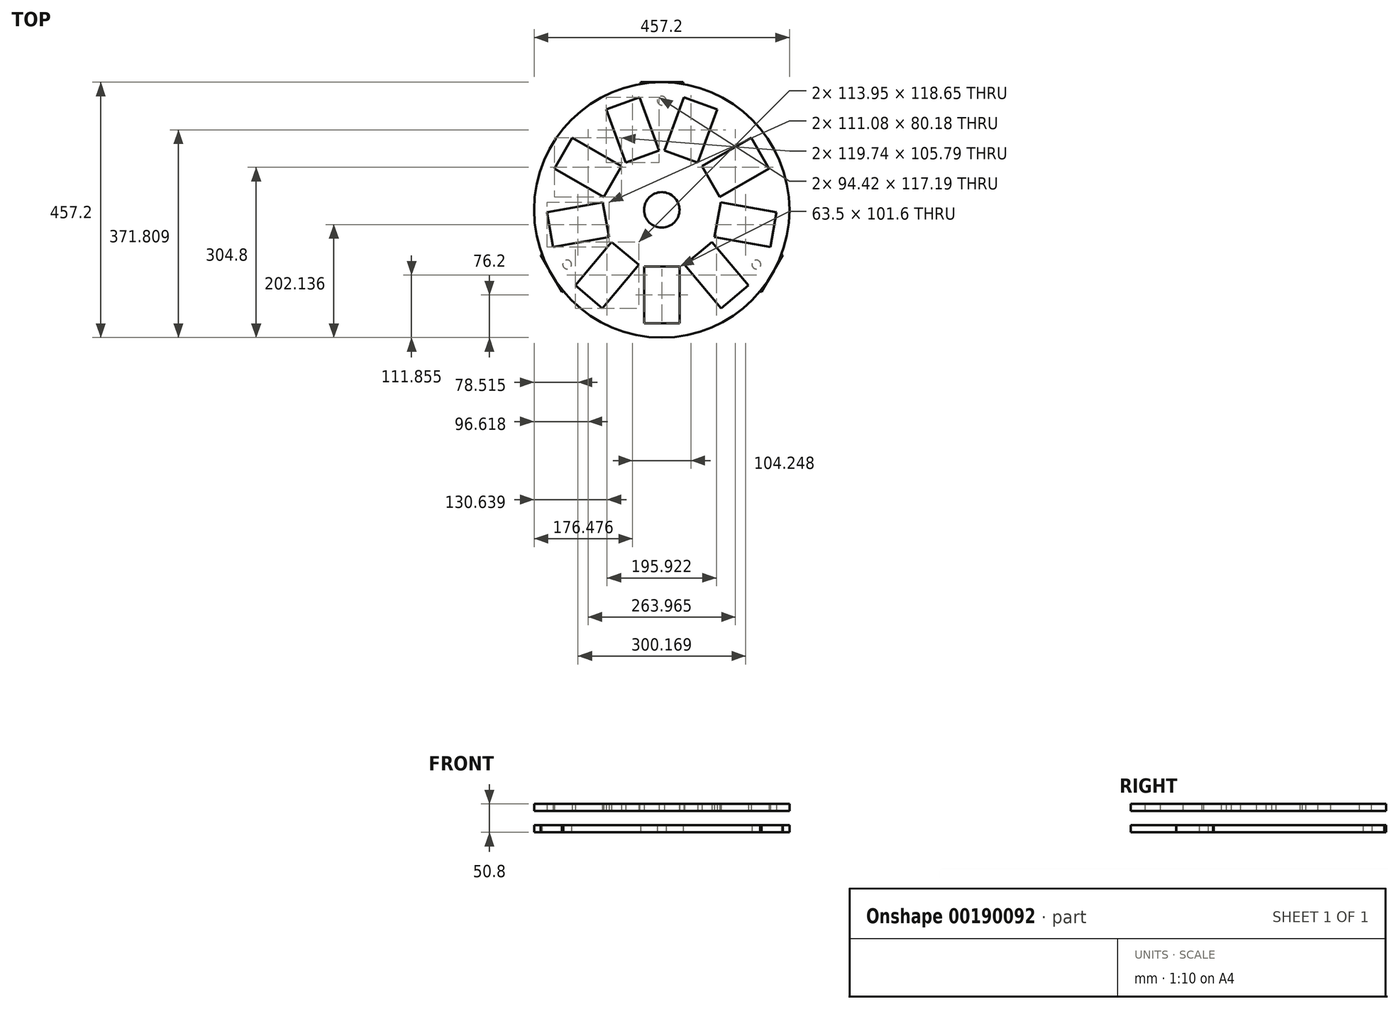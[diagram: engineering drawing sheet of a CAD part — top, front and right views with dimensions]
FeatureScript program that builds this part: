
annotation { "Feature Type Name" : "Feature", "Feature Type Description" : "" }
export const myFeature = defineFeature(function(context is Context, id is Id, definition is map)
    precondition{}
    {
        {
            var Q0;
            Q0=qCreatedBy(makeId("Top.planeOp"),FACE);
            var sketch = newSketch(context, id + "F0", { "sketchPlane" : qUnion([Q0])});
            skArc(sketch, "E0", {"start": v(-38.1, 147.56) * mm, "mid": v(-131.98, 76.2) * mm, "end": v(-146.84, -40.78) * mm});
            skLineSegment(sketch, "E1.top", {"start": v(-38.1, 228.6) * mm, "end": v(38.1, 228.6) * mm});
            skLineSegment(sketch, "E1.left", {"start": v(-38.1, 147.56) * mm, "end": v(-38.1, 228.6) * mm});
            skLineSegment(sketch, "E1.right", {"start": v(38.1, 147.56) * mm, "end": v(38.1, 228.6) * mm});
            skCircle(sketch, "E2", {"center": v(0, 195.58) * mm, "radius": 7.94 * mm});
            skPoint(sketch, "E1.bottom.start.orphan", {"position": v(-38.1, 0) * mm});
            skLineSegment(sketch, "E3.1.0", {"start": v(-178.92, -147.3) * mm, "end": v(-217.02, -81.3) * mm});
            skCircle(sketch, "E3.1.1", {"center": v(-169.38, -97.79) * mm, "radius": 7.94 * mm});
            skLineSegment(sketch, "E3.1.2", {"start": v(-146.84, -40.78) * mm, "end": v(-217.02, -81.3) * mm});
            skLineSegment(sketch, "E3.1.3", {"start": v(-108.74, -106.78) * mm, "end": v(-178.92, -147.3) * mm});
            skLineSegment(sketch, "E3.2.0", {"start": v(217.02, -81.3) * mm, "end": v(178.92, -147.3) * mm});
            skCircle(sketch, "E3.2.1", {"center": v(169.38, -97.8) * mm, "radius": 7.94 * mm});
            skLineSegment(sketch, "E3.2.2", {"start": v(108.74, -106.78) * mm, "end": v(178.92, -147.3) * mm});
            skLineSegment(sketch, "E3.2.3", {"start": v(146.84, -40.78) * mm, "end": v(217.02, -81.3) * mm});
            skArc(sketch, "E4.trimOffspring", {"start": v(-108.74, -106.78) * mm, "mid": v(0, -152.4) * mm, "end": v(108.74, -106.78) * mm});
            skArc(sketch, "E5.trimOffspring", {"start": v(146.84, -40.78) * mm, "mid": v(131.98, 76.2) * mm, "end": v(38.1, 147.56) * mm});
            skCircle(sketch, "E6", {"center": v(0, 0) * mm, "radius": 228.6 * mm});
            skSolve(sketch);
        }
        {
            var Q0;
            Q0 = qSketchRegion(id + "F0", true);
            extrude(context, id + "F1", {"entities" : qUnion([Q0]), "depth" : 12.7 * mm});
        }
        {
            var Q0;
            Q0=makeQuery(id+"F1.opExtrude","CAP_FACE",FACE,{"disambiguationData":[OSD([sQuery(id+"F0.wireOp",EDGE,"E1.top"),sQuery(id+"F0.wireOp",EDGE,"E1.left"),sQuery(id+"F0.wireOp",EDGE,"E1.right"),sQuery(id+"F0.wireOp",EDGE,"E2"),sQuery(id+"F0.wireOp",EDGE,"E3.1.0"),sQuery(id+"F0.wireOp",EDGE,"E3.1.1"),sQuery(id+"F0.wireOp",EDGE,"E3.1.2"),sQuery(id+"F0.wireOp",EDGE,"E3.1.3"),sQuery(id+"F0.wireOp",EDGE,"E3.2.0"),sQuery(id+"F0.wireOp",EDGE,"E3.2.1"),sQuery(id+"F0.wireOp",EDGE,"E3.2.2"),sQuery(id+"F0.wireOp",EDGE,"E3.2.3"),sQuery(id+"F0.wireOp",EDGE,"E6")])],"isStart":false});
            var sketch = newSketch(context, id + "F2", { "sketchPlane" : qUnion([Q0])});
            skPoint(sketch, "E7.middle", {"position": v(39.44, 147.2) * mm});
            skLineSegment(sketch, "E8", {"start": v(26.3, 98.14) * mm, "end": v(-4.37, 106.36) * mm});
            skLineSegment(sketch, "E9", {"start": v(-4.37, 106.36) * mm, "end": v(21.92, 204.5) * mm});
            skLineSegment(sketch, "E10", {"start": v(21.92, 204.5) * mm, "end": v(83.26, 188.06) * mm});
            skLineSegment(sketch, "E11", {"start": v(83.26, 188.06) * mm, "end": v(56.96, 89.92) * mm});
            skLineSegment(sketch, "E12", {"start": v(56.96, 89.92) * mm, "end": v(56.96, 89.9) * mm});
            skLineSegment(sketch, "E13", {"start": v(56.96, 89.9) * mm, "end": v(26.3, 98.14) * mm});
            skLineSegment(sketch, "E14.1.0", {"start": v(-57.1, 197.58) * mm, "end": v(-14.16, 105.5) * mm});
            skLineSegment(sketch, "E14.1.1", {"start": v(-114.65, 170.74) * mm, "end": v(-57.1, 197.58) * mm});
            skLineSegment(sketch, "E14.1.2", {"start": v(-71.71, 78.66) * mm, "end": v(-114.65, 170.74) * mm});
            skLineSegment(sketch, "E14.1.3", {"start": v(-14.16, 105.48) * mm, "end": v(-42.94, 92.08) * mm});
            skLineSegment(sketch, "E14.1.4", {"start": v(-42.94, 92.08) * mm, "end": v(-71.71, 78.66) * mm});
            skLineSegment(sketch, "E14.2.0", {"start": v(-170.74, 114.65) * mm, "end": v(-78.66, 71.71) * mm});
            skLineSegment(sketch, "E14.2.1", {"start": v(-197.58, 57.1) * mm, "end": v(-170.74, 114.65) * mm});
            skLineSegment(sketch, "E14.2.2", {"start": v(-105.5, 14.16) * mm, "end": v(-197.58, 57.1) * mm});
            skLineSegment(sketch, "E14.2.3", {"start": v(-78.65, 71.7) * mm, "end": v(-92.08, 42.94) * mm});
            skLineSegment(sketch, "E14.2.4", {"start": v(-92.08, 42.94) * mm, "end": v(-105.5, 14.16) * mm});
            skLineSegment(sketch, "E14.3.0", {"start": v(-204.5, -21.92) * mm, "end": v(-106.36, 4.37) * mm});
            skLineSegment(sketch, "E14.3.1", {"start": v(-188.06, -83.26) * mm, "end": v(-204.5, -21.92) * mm});
            skLineSegment(sketch, "E14.3.2", {"start": v(-89.92, -56.96) * mm, "end": v(-188.06, -83.26) * mm});
            skLineSegment(sketch, "E14.3.3", {"start": v(-106.34, 4.38) * mm, "end": v(-98.14, -26.3) * mm});
            skLineSegment(sketch, "E14.3.4", {"start": v(-98.14, -26.3) * mm, "end": v(-89.92, -56.96) * mm});
            skLineSegment(sketch, "E14.4.0", {"start": v(-142.56, -148.24) * mm, "end": v(-84.28, -65.01) * mm});
            skLineSegment(sketch, "E14.4.1", {"start": v(-90.54, -184.66) * mm, "end": v(-142.56, -148.24) * mm});
            skLineSegment(sketch, "E14.4.2", {"start": v(-32.27, -101.44) * mm, "end": v(-90.54, -184.66) * mm});
            skLineSegment(sketch, "E14.4.3", {"start": v(-84.27, -65) * mm, "end": v(-58.28, -83.23) * mm});
            skLineSegment(sketch, "E14.4.4", {"start": v(-58.28, -83.23) * mm, "end": v(-32.27, -101.44) * mm});
            skLineSegment(sketch, "E14.5.0", {"start": v(-13.92, -205.2) * mm, "end": v(-22.77, -103.98) * mm});
            skLineSegment(sketch, "E14.5.1", {"start": v(49.34, -199.66) * mm, "end": v(-13.92, -205.2) * mm});
            skLineSegment(sketch, "E14.5.2", {"start": v(40.48, -98.45) * mm, "end": v(49.34, -199.66) * mm});
            skLineSegment(sketch, "E14.5.3", {"start": v(-22.78, -103.96) * mm, "end": v(8.86, -101.21) * mm});
            skLineSegment(sketch, "E14.5.4", {"start": v(8.86, -101.21) * mm, "end": v(40.48, -98.45) * mm});
            skLineSegment(sketch, "E14.6.0", {"start": v(121.23, -166.13) * mm, "end": v(49.4, -94.3) * mm});
            skLineSegment(sketch, "E14.6.1", {"start": v(166.13, -121.23) * mm, "end": v(121.23, -166.13) * mm});
            skLineSegment(sketch, "E14.6.2", {"start": v(94.3, -49.4) * mm, "end": v(166.13, -121.23) * mm});
            skLineSegment(sketch, "E14.6.3", {"start": v(49.38, -94.28) * mm, "end": v(71.84, -71.84) * mm});
            skLineSegment(sketch, "E14.6.4", {"start": v(71.84, -71.84) * mm, "end": v(94.3, -49.4) * mm});
            skLineSegment(sketch, "E14.7.0", {"start": v(199.66, -49.34) * mm, "end": v(98.45, -40.48) * mm});
            skLineSegment(sketch, "E14.7.1", {"start": v(205.2, 13.92) * mm, "end": v(199.66, -49.34) * mm});
            skLineSegment(sketch, "E14.7.2", {"start": v(103.98, 22.77) * mm, "end": v(205.2, 13.92) * mm});
            skLineSegment(sketch, "E14.7.3", {"start": v(98.43, -40.48) * mm, "end": v(101.21, -8.86) * mm});
            skLineSegment(sketch, "E14.7.4", {"start": v(101.21, -8.86) * mm, "end": v(103.98, 22.77) * mm});
            skLineSegment(sketch, "E14.8.0", {"start": v(184.66, 90.54) * mm, "end": v(101.44, 32.27) * mm});
            skLineSegment(sketch, "E14.8.1", {"start": v(148.24, 142.56) * mm, "end": v(184.66, 90.54) * mm});
            skLineSegment(sketch, "E14.8.2", {"start": v(65.01, 84.28) * mm, "end": v(148.24, 142.56) * mm});
            skLineSegment(sketch, "E14.8.3", {"start": v(101.42, 32.26) * mm, "end": v(83.23, 58.28) * mm});
            skLineSegment(sketch, "E14.8.4", {"start": v(83.23, 58.28) * mm, "end": v(65.01, 84.28) * mm});
            skPoint(sketch, "E14.center", {"position": v(0, 0) * mm});
            skCircle(sketch, "E15", {"center": v(0, 0) * mm, "radius": 228.6 * mm});
            skSolve(sketch);
        }
        {
            var Q0;
            {var subQ13=sQuery(id+"F2.wireOp",EDGE,"E14.1.1");Q0=makeQuery(id+"F2.imprint","IMPRINT",FACE,{"disambiguationData":[TD([[makeQuery(id+"F2.imprint","IMPRINT",EDGE,{"derivedFrom":subQ13}),1.0]])]});}
            var Q1;
            {var subQ17=sQuery(id+"F2.wireOp",EDGE,"E14.4.1");Q1=makeQuery(id+"F2.imprint","IMPRINT",FACE,{"disambiguationData":[TD([[makeQuery(id+"F2.imprint","IMPRINT",EDGE,{"derivedFrom":subQ17}),1.0]])]});}
            var Q2;
            {var subQ18=sQuery(id+"F2.wireOp",EDGE,"E14.7.1");Q2=makeQuery(id+"F2.imprint","IMPRINT",FACE,{"disambiguationData":[TD([[makeQuery(id+"F2.imprint","IMPRINT",EDGE,{"derivedFrom":subQ18}),1.0]])]});}
            var Q3;
            {var subQ0=sQuery(id+"F2.wireOp",EDGE,"E14.8.1");Q3=makeQuery(id+"F2.imprint","IMPRINT",FACE,{"disambiguationData":[TD([[makeQuery(id+"F2.imprint","IMPRINT",EDGE,{"derivedFrom":subQ0}),-1.0]])]});}
            var Q4;
            {var subQ0=sQuery(id+"F2.wireOp",EDGE,"E14.7.1");Q4=makeQuery(id+"F2.imprint","IMPRINT",FACE,{"disambiguationData":[TD([[makeQuery(id+"F2.imprint","IMPRINT",EDGE,{"derivedFrom":subQ0}),-1.0]])]});}
            var Q5;
            {var subQ0=sQuery(id+"F2.wireOp",EDGE,"E11");var subQ1=sQuery(id+"F2.wireOp",EDGE,"E10");var subQ2=makeQuery(id+"F2.imprint","INTERSECT",VERTEX,{"derivedFrom":[subQ1,subQ0]});Q5=makeQuery(id+"F2.imprint","IMPRINT",FACE,{"disambiguationData":[TD([[makeQuery(id+"F2.imprint","IMPRINT",EDGE,{"disambiguationData":[TD([[subQ2,1.0]])],"derivedFrom":subQ1}),-1.0]])]});}
            var Q6;
            {var subQ0=sQuery(id+"F2.wireOp",EDGE,"E14.6.1");var subQ1=sQuery(id+"F2.wireOp",EDGE,"E14.6.0");var subQ2=makeQuery(id+"F2.imprint","INTERSECT",VERTEX,{"derivedFrom":[subQ1,subQ0]});Q6=makeQuery(id+"F2.imprint","IMPRINT",FACE,{"disambiguationData":[TD([[makeQuery(id+"F2.imprint","IMPRINT",EDGE,{"disambiguationData":[TD([[subQ2,1.0]])],"derivedFrom":subQ0}),-1.0]])]});}
            var Q7;
            {var subQ0=sQuery(id+"F2.wireOp",EDGE,"E14.5.1");Q7=makeQuery(id+"F2.imprint","IMPRINT",FACE,{"disambiguationData":[TD([[makeQuery(id+"F2.imprint","IMPRINT",EDGE,{"derivedFrom":subQ0}),-1.0]])]});}
            var Q8;
            {var subQ0=sQuery(id+"F2.wireOp",EDGE,"E14.4.1");Q8=makeQuery(id+"F2.imprint","IMPRINT",FACE,{"disambiguationData":[TD([[makeQuery(id+"F2.imprint","IMPRINT",EDGE,{"derivedFrom":subQ0}),-1.0]])]});}
            var Q9;
            {var subQ0=sQuery(id+"F2.wireOp",EDGE,"E14.3.1");var subQ1=sQuery(id+"F2.wireOp",EDGE,"E14.3.0");var subQ2=makeQuery(id+"F2.imprint","INTERSECT",VERTEX,{"derivedFrom":[subQ1,subQ0]});Q9=makeQuery(id+"F2.imprint","IMPRINT",FACE,{"disambiguationData":[TD([[makeQuery(id+"F2.imprint","IMPRINT",EDGE,{"disambiguationData":[TD([[subQ2,1.0]])],"derivedFrom":subQ0}),-1.0]])]});}
            var Q10;
            {var subQ0=sQuery(id+"F2.wireOp",EDGE,"E14.2.1");Q10=makeQuery(id+"F2.imprint","IMPRINT",FACE,{"disambiguationData":[TD([[makeQuery(id+"F2.imprint","IMPRINT",EDGE,{"derivedFrom":subQ0}),-1.0]])]});}
            var Q11;
            {var subQ0=sQuery(id+"F2.wireOp",EDGE,"E14.1.1");Q11=makeQuery(id+"F2.imprint","IMPRINT",FACE,{"disambiguationData":[TD([[makeQuery(id+"F2.imprint","IMPRINT",EDGE,{"derivedFrom":subQ0}),-1.0]])]});}
            extrude(context, id + "F3", {"entities" : qUnion([Q0, Q1, Q2, Q3, Q4, Q5, Q6, Q7, Q8, Q9, Q10, Q11]), "operationType" : NewBodyOperationType.ADD, "oppositeDirection" : true, "depth" : 12.7 * mm});
        }
        {
            var Q0;
            Q0=makeQuery(id+"F2.imprint","IMPRINT",FACE,{"disambiguationData":[TD([[makeQuery(id+"F2.imprint","IMPRINT",EDGE,{"derivedFrom":sQuery(id+"F2.wireOp",EDGE,"E8")}),1.0]])]});
            cPlane(context, id + "F4", {"entities" : qUnion([Q0]), "cplaneType" : CPlaneType.OFFSET, "offset" : 25.4 * mm, "width" : 152.4 * mm, "height" : 152.4 * mm});
        }
        {
            var Q0;
            Q0=qCreatedBy(id+"F4.planeOp",FACE);
            var sketch = newSketch(context, id + "F5", { "sketchPlane" : qUnion([Q0])});
            skCircle(sketch, "E16", {"center": v(0, 0) * mm, "radius": 228.6 * mm});
            skLineSegment(sketch, "E17", {"start": v(0, 0) * mm, "end": v(0, -308.84) * mm});
            skLineSegment(sketch, "E18", {"start": v(0, 0) * mm, "end": v(-183.15, -218.27) * mm});
            skCircle(sketch, "E19", {"center": v(0, 0) * mm, "radius": 152.4 * mm});
            skLineSegment(sketch, "E20", {"start": v(-97.96, -116.75) * mm, "end": v(-65.3, -77.83) * mm});
            skLineSegment(sketch, "E21", {"start": v(-65.3, -77.83) * mm, "end": v(-40.99, -98.24) * mm});
            skLineSegment(sketch, "E22", {"start": v(-40.99, -98.24) * mm, "end": v(-106.3, -176.07) * mm});
            skLineSegment(sketch, "E23", {"start": v(-106.3, -176.07) * mm, "end": v(-154.94, -135.25) * mm});
            skLineSegment(sketch, "E24", {"start": v(-154.94, -135.25) * mm, "end": v(-89.63, -57.42) * mm});
            skLineSegment(sketch, "E25", {"start": v(-89.63, -57.42) * mm, "end": v(-65.3, -77.83) * mm});
            skLineSegment(sketch, "E26.1.0", {"start": v(31.75, -101.6) * mm, "end": v(31.75, -203.2) * mm});
            skLineSegment(sketch, "E26.1.1", {"start": v(31.75, -203.2) * mm, "end": v(-31.75, -203.2) * mm});
            skLineSegment(sketch, "E26.1.2", {"start": v(-31.75, -203.2) * mm, "end": v(-31.75, -101.6) * mm});
            skLineSegment(sketch, "E26.1.3", {"start": v(-31.75, -101.6) * mm, "end": v(0, -101.6) * mm});
            skLineSegment(sketch, "E26.1.4", {"start": v(0, -101.6) * mm, "end": v(31.75, -101.6) * mm});
            skLineSegment(sketch, "E26.2.0", {"start": v(89.63, -57.42) * mm, "end": v(154.94, -135.25) * mm});
            skLineSegment(sketch, "E26.2.1", {"start": v(154.94, -135.25) * mm, "end": v(106.3, -176.07) * mm});
            skLineSegment(sketch, "E26.2.2", {"start": v(106.3, -176.07) * mm, "end": v(40.99, -98.24) * mm});
            skLineSegment(sketch, "E26.2.3", {"start": v(40.99, -98.24) * mm, "end": v(65.3, -77.83) * mm});
            skLineSegment(sketch, "E26.2.4", {"start": v(65.3, -77.83) * mm, "end": v(89.63, -57.42) * mm});
            skLineSegment(sketch, "E26.3.0", {"start": v(105.57, 13.62) * mm, "end": v(205.63, -4.02) * mm});
            skLineSegment(sketch, "E26.3.1", {"start": v(205.63, -4.02) * mm, "end": v(194.6, -66.55) * mm});
            skLineSegment(sketch, "E26.3.2", {"start": v(194.6, -66.55) * mm, "end": v(94.54, -48.91) * mm});
            skLineSegment(sketch, "E26.3.3", {"start": v(94.54, -48.91) * mm, "end": v(100.06, -17.64) * mm});
            skLineSegment(sketch, "E26.3.4", {"start": v(100.06, -17.64) * mm, "end": v(105.57, 13.62) * mm});
            skLineSegment(sketch, "E26.4.0", {"start": v(72.11, 78.3) * mm, "end": v(160.1, 129.1) * mm});
            skLineSegment(sketch, "E26.4.1", {"start": v(160.1, 129.1) * mm, "end": v(191.85, 74.1) * mm});
            skLineSegment(sketch, "E26.4.2", {"start": v(191.85, 74.1) * mm, "end": v(103.86, 23.3) * mm});
            skLineSegment(sketch, "E26.4.3", {"start": v(103.86, 23.3) * mm, "end": v(87.99, 50.8) * mm});
            skLineSegment(sketch, "E26.4.4", {"start": v(87.99, 50.8) * mm, "end": v(72.11, 78.3) * mm});
            skLineSegment(sketch, "E26.5.0", {"start": v(4.91, 106.33) * mm, "end": v(39.66, 201.8) * mm});
            skLineSegment(sketch, "E26.5.1", {"start": v(39.66, 201.8) * mm, "end": v(99.33, 180.09) * mm});
            skLineSegment(sketch, "E26.5.2", {"start": v(99.33, 180.09) * mm, "end": v(64.58, 84.61) * mm});
            skLineSegment(sketch, "E26.5.3", {"start": v(64.58, 84.61) * mm, "end": v(34.75, 95.47) * mm});
            skLineSegment(sketch, "E26.5.4", {"start": v(34.75, 95.47) * mm, "end": v(4.91, 106.33) * mm});
            skLineSegment(sketch, "E26.6.0", {"start": v(-64.58, 84.61) * mm, "end": v(-99.33, 180.09) * mm});
            skLineSegment(sketch, "E26.6.1", {"start": v(-99.33, 180.09) * mm, "end": v(-39.66, 201.8) * mm});
            skLineSegment(sketch, "E26.6.2", {"start": v(-39.66, 201.8) * mm, "end": v(-4.91, 106.33) * mm});
            skLineSegment(sketch, "E26.6.3", {"start": v(-4.91, 106.33) * mm, "end": v(-34.75, 95.47) * mm});
            skLineSegment(sketch, "E26.6.4", {"start": v(-34.75, 95.47) * mm, "end": v(-64.58, 84.61) * mm});
            skLineSegment(sketch, "E26.7.0", {"start": v(-103.86, 23.3) * mm, "end": v(-191.85, 74.1) * mm});
            skLineSegment(sketch, "E26.7.1", {"start": v(-191.85, 74.1) * mm, "end": v(-160.1, 129.1) * mm});
            skLineSegment(sketch, "E26.7.2", {"start": v(-160.1, 129.1) * mm, "end": v(-72.11, 78.3) * mm});
            skLineSegment(sketch, "E26.7.3", {"start": v(-72.11, 78.3) * mm, "end": v(-87.99, 50.8) * mm});
            skLineSegment(sketch, "E26.7.4", {"start": v(-87.99, 50.8) * mm, "end": v(-103.86, 23.3) * mm});
            skLineSegment(sketch, "E26.8.0", {"start": v(-94.54, -48.91) * mm, "end": v(-194.6, -66.55) * mm});
            skLineSegment(sketch, "E26.8.1", {"start": v(-194.6, -66.55) * mm, "end": v(-205.63, -4.02) * mm});
            skLineSegment(sketch, "E26.8.2", {"start": v(-205.63, -4.02) * mm, "end": v(-105.57, 13.62) * mm});
            skLineSegment(sketch, "E26.8.3", {"start": v(-105.57, 13.62) * mm, "end": v(-100.06, -17.64) * mm});
            skLineSegment(sketch, "E26.8.4", {"start": v(-100.06, -17.64) * mm, "end": v(-94.54, -48.91) * mm});
            skSolve(sketch);
        }
        {
            var Q0;
            Q0 = qSketchRegion(id + "F5", true);
            var Q1;
            {var subQ3=sQuery(id+"F5.wireOp",EDGE,"E21");Q1=makeQuery(id+"F5.imprint","IMPRINT",FACE,{"disambiguationData":[TD([[makeQuery(id+"F5.imprint","IMPRINT",EDGE,{"derivedFrom":subQ3}),1.0]])]});}
            var Q2;
            {var subQ35=sQuery(id+"F5.wireOp",EDGE,"E25");Q2=makeQuery(id+"F5.imprint","IMPRINT",FACE,{"disambiguationData":[TD([[makeQuery(id+"F5.imprint","IMPRINT",EDGE,{"derivedFrom":subQ35}),1.0]])]});}
            extrude(context, id + "F6", {"entities" : qUnion([Q0, Q1, Q2]), "depth" : 12.7 * mm});
        }
        {
            var Q0;
            Q0=makeQuery(id+"F6.opExtrude","CAP_FACE",FACE,{"disambiguationData":[OSD([sQuery(id+"F5.wireOp",EDGE,"E16"),sQuery(id+"F5.wireOp",EDGE,"E21"),sQuery(id+"F5.wireOp",EDGE,"E22"),sQuery(id+"F5.wireOp",EDGE,"E23"),sQuery(id+"F5.wireOp",EDGE,"E24"),sQuery(id+"F5.wireOp",EDGE,"E25"),sQuery(id+"F5.wireOp",EDGE,"E26.1.0"),sQuery(id+"F5.wireOp",EDGE,"E26.1.1"),sQuery(id+"F5.wireOp",EDGE,"E26.1.2"),sQuery(id+"F5.wireOp",EDGE,"E26.1.3"),sQuery(id+"F5.wireOp",EDGE,"E26.1.4"),sQuery(id+"F5.wireOp",EDGE,"E26.2.0"),sQuery(id+"F5.wireOp",EDGE,"E26.2.1"),sQuery(id+"F5.wireOp",EDGE,"E26.2.2"),sQuery(id+"F5.wireOp",EDGE,"E26.2.3"),sQuery(id+"F5.wireOp",EDGE,"E26.2.4"),sQuery(id+"F5.wireOp",EDGE,"E26.3.0"),sQuery(id+"F5.wireOp",EDGE,"E26.3.1"),sQuery(id+"F5.wireOp",EDGE,"E26.3.2"),sQuery(id+"F5.wireOp",EDGE,"E26.3.3"),sQuery(id+"F5.wireOp",EDGE,"E26.3.4"),sQuery(id+"F5.wireOp",EDGE,"E26.4.0"),sQuery(id+"F5.wireOp",EDGE,"E26.4.1"),sQuery(id+"F5.wireOp",EDGE,"E26.4.2"),sQuery(id+"F5.wireOp",EDGE,"E26.4.3"),sQuery(id+"F5.wireOp",EDGE,"E26.4.4"),sQuery(id+"F5.wireOp",EDGE,"E26.5.0"),sQuery(id+"F5.wireOp",EDGE,"E26.5.1"),sQuery(id+"F5.wireOp",EDGE,"E26.5.2"),sQuery(id+"F5.wireOp",EDGE,"E26.5.3"),sQuery(id+"F5.wireOp",EDGE,"E26.5.4"),sQuery(id+"F5.wireOp",EDGE,"E26.6.0"),sQuery(id+"F5.wireOp",EDGE,"E26.6.1"),sQuery(id+"F5.wireOp",EDGE,"E26.6.2"),sQuery(id+"F5.wireOp",EDGE,"E26.6.3"),sQuery(id+"F5.wireOp",EDGE,"E26.6.4"),sQuery(id+"F5.wireOp",EDGE,"E26.7.0"),sQuery(id+"F5.wireOp",EDGE,"E26.7.1"),sQuery(id+"F5.wireOp",EDGE,"E26.7.2"),sQuery(id+"F5.wireOp",EDGE,"E26.7.3"),sQuery(id+"F5.wireOp",EDGE,"E26.7.4"),sQuery(id+"F5.wireOp",EDGE,"E26.8.0"),sQuery(id+"F5.wireOp",EDGE,"E26.8.1"),sQuery(id+"F5.wireOp",EDGE,"E26.8.2"),sQuery(id+"F5.wireOp",EDGE,"E26.8.3"),sQuery(id+"F5.wireOp",EDGE,"E26.8.4")])],"isStart":false});
            var sketch = newSketch(context, id + "F7", { "sketchPlane" : qUnion([Q0])});
            skCircle(sketch, "E27", {"center": v(0, 0) * mm, "radius": 31.75 * mm});
            skSolve(sketch);
        }
        {
            var Q0;
            Q0 = qSketchRegion(id + "F7", true);
            extrude(context, id + "F8", {"entities" : qUnion([Q0]), "operationType" : NewBodyOperationType.REMOVE, "oppositeDirection" : true, "depth" : 25.4 * mm});
        }
    });
